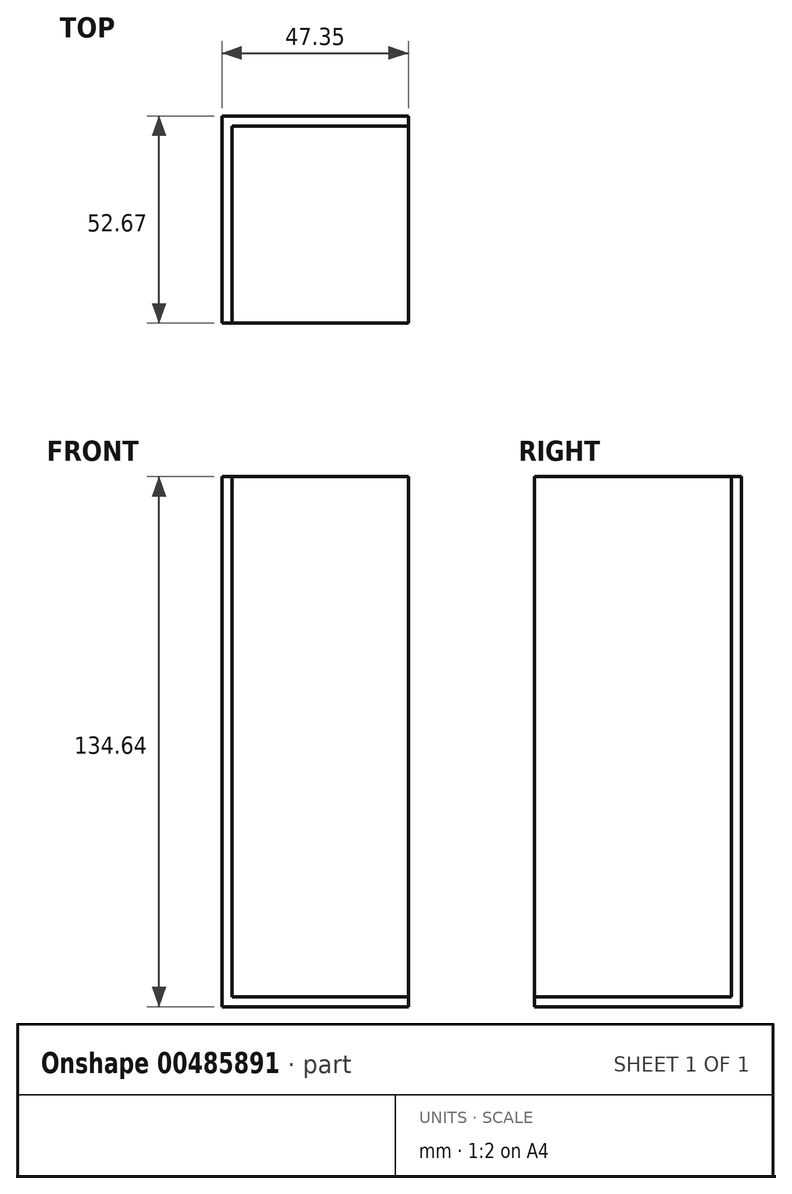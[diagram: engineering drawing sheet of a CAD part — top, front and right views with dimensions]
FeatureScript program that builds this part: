
annotation { "Feature Type Name" : "Feature", "Feature Type Description" : "" }
export const myFeature = defineFeature(function(context is Context, id is Id, definition is map)
    precondition{}
    {
        {
            var Q0;
            Q0=qCreatedBy(makeId("Top.planeOp"),FACE);
            var sketch = newSketch(context, id + "F0", { "sketchPlane" : qUnion([Q0])});
            skLineSegment(sketch, "E0.bottom", {"start": v(47.35, 52.67) * mm, "end": v(0, 52.67) * mm});
            skLineSegment(sketch, "E0.top", {"start": v(47.35, 0) * mm, "end": v(0, 0) * mm});
            skLineSegment(sketch, "E0.left", {"start": v(47.35, 52.67) * mm, "end": v(47.35, 0) * mm});
            skLineSegment(sketch, "E0.right", {"start": v(0, 52.67) * mm, "end": v(0, 0) * mm});
            skSolve(sketch);
        }
        {
            var Q0;
            Q0=makeQuery(id+"F0.imprint","IMPRINT",FACE,{"disambiguationData":[TD([[makeQuery(id+"F0.imprint","IMPRINT",EDGE,{"derivedFrom":sQuery(id+"F0.wireOp",EDGE,"E0.bottom")}),1.0]])]});
            extrude(context, id + "F1", {"entities" : qUnion([Q0]), "depth" : 134.64 * mm});
        }
        {
            var Q0;
            Q0=makeQuery(id+"F1.opExtrude","SWEPT_FACE",FACE,{"disambiguationData":[OSD([sQuery(id+"F0.wireOp",EDGE,"E0.top")])]});
            var Q1;
            Q1=makeQuery(id+"F1.opExtrude","SWEPT_FACE",FACE,{"disambiguationData":[OSD([sQuery(id+"F0.wireOp",EDGE,"E0.left")])]});
            var Q2;
            Q2=makeQuery(id+"F1.opExtrude","CAP_FACE",FACE,{"disambiguationData":[OSD([sQuery(id+"F0.wireOp",EDGE,"E0.bottom"),sQuery(id+"F0.wireOp",EDGE,"E0.top"),sQuery(id+"F0.wireOp",EDGE,"E0.left"),sQuery(id+"F0.wireOp",EDGE,"E0.right")])],"isStart":false});
            shell(context, id + "F2", {"entities" : qUnion([Q0, Q1, Q2]), "thickness" : 2.54 * mm});
        }
        {
            var Q0;
            Q0=makeQuery(id+"F2.opShell","OFFSET_FACE",FACE,{"disambiguationData":[OSD([sQuery(id+"F0.wireOp",EDGE,"E0.right")])]});
            var Q1;
            Q1=makeQuery(id+"F2.opShell","OFFSET_FACE",FACE,{"disambiguationData":[OSD([sQuery(id+"F0.wireOp",EDGE,"E0.bottom")])]});
            var Q2;
            Q2=makeQuery(id+"F2.opShell","OFFSET_FACE",FACE,{"disambiguationData":[OSD([sQuery(id+"F0.wireOp",EDGE,"E0.bottom"),sQuery(id+"F0.wireOp",EDGE,"E0.top"),sQuery(id+"F0.wireOp",EDGE,"E0.left"),sQuery(id+"F0.wireOp",EDGE,"E0.right")])]});
            shell(context, id + "F3", {"entities" : qUnion([Q0, Q1, Q2]), "thickness" : 2.54 * mm});
        }
    });
